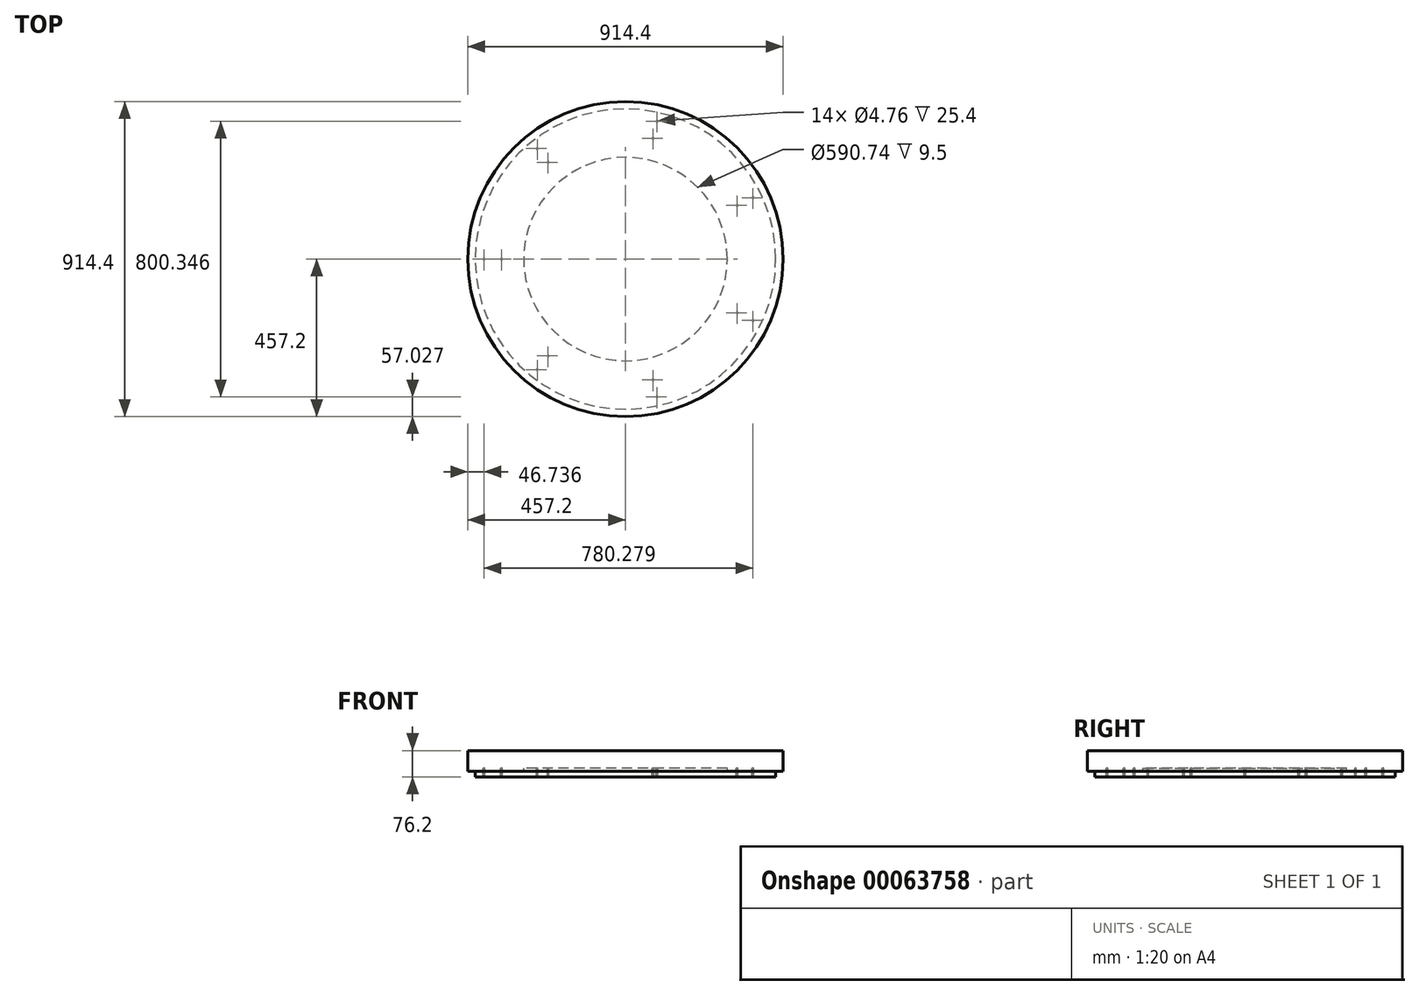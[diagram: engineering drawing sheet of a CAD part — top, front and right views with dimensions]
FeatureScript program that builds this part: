
annotation { "Feature Type Name" : "Feature", "Feature Type Description" : "" }
export const myFeature = defineFeature(function(context is Context, id is Id, definition is map)
    precondition{}
    {
        {
            assignVariable(context, id + "F0", {"name" : "H", "anyValue" : 15});
        }
        {
            assignVariable(context, id + "F1", {"name" : "S", "anyValue" : 7});
        }
        {
            var Q0;
            Q0=qCreatedBy(makeId("Top.planeOp"),FACE);
            var sketch = newSketch(context, id + "F2", { "sketchPlane" : qUnion([Q0])});
            skCircle(sketch, "E0", {"center": v(0, 0) * mm, "radius": 457.2 * mm});
            skCircle(sketch, "E1", {"center": v(0, 0) * mm, "radius": 444.5 * mm});
            skCircle(sketch, "E2.0", {"center": v(0, 0) * mm, "radius": 435.86 * mm});
            skSolve(sketch);
        }
        {
            var Q0;
            Q0=makeQuery(id+"F2.imprint","IMPRINT",FACE,{"disambiguationData":[TD([[makeQuery(id+"F2.imprint","IMPRINT",EDGE,{"derivedFrom":sQuery(id+"F2.wireOp",EDGE,"E1")}),1.0]])]});
            var Q1;
            Q1=sQuery(id+"F2.wireOp",EDGE,"E1");
            var Q2;
            Q2=sQuery(id+"F2.wireOp",EDGE,"E2.0");
            extrude(context, id + "F3", {"entities" : qUnion([Q0]), "surfaceEntities" : qUnion([Q1, Q2]), "depth" : (getVariable(context, 'H') - 5.5) * mm});
        }
        {
            var Q0;
            Q0=makeQuery(id+"F3.opExtrude","CAP_FACE",FACE,{"disambiguationData":[OSD([sQuery(id+"F2.wireOp",EDGE,"E1"),sQuery(id+"F2.wireOp",EDGE,"E2.0")])],"isStart":false});
            var sketch = newSketch(context, id + "F4", { "sketchPlane" : qUnion([Q0])});
            skCircle(sketch, "E3.0", {"center": v(0, 0) * mm, "radius": 435.86 * mm});
            skSolve(sketch);
        }
        {
            var Q0;
            Q0=qSketchRegion(id+"F4",true);
            extrude(context, id + "F5", {"entities" : qUnion([Q0]), "oppositeDirection" : true, "depth" : 25.4 * mm});
        }
        {
            var Q0;
            Q0=makeQuery(id+"F5.opExtrude","CAP_FACE",FACE,{"disambiguationData":[OSD([sQuery(id+"F4.wireOp",EDGE,"E3.0")])],"isStart":true});
            var sketch = newSketch(context, id + "F6", { "sketchPlane" : qUnion([Q0])});
            skLineSegment(sketch, "E4", {"start": v(-435.86, 0) * mm, "end": v(0, 0) * mm, "construction": true});
            skCircle(sketch, "E5.0", {"center": v(0, 0) * mm, "radius": 410.46 * mm, "construction": true});
            skCircle(sketch, "E6.0", {"center": v(0, 0) * mm, "radius": 359.66 * mm, "construction": true});
            skPoint(sketch, "E7", {"position": v(-410.46, 0) * mm});
            skPoint(sketch, "E8", {"position": v(-359.66, 0) * mm});
            skPoint(sketch, "E9.1.0", {"position": v(-224.25, -281.2) * mm});
            skPoint(sketch, "E9.1.1", {"position": v(-255.92, -320.91) * mm});
            skPoint(sketch, "E9.2.0", {"position": v(80.03, -350.65) * mm});
            skPoint(sketch, "E9.2.1", {"position": v(91.34, -400.17) * mm});
            skPoint(sketch, "E9.3.0", {"position": v(324.05, -156.05) * mm});
            skPoint(sketch, "E9.3.1", {"position": v(369.82, -178.1) * mm});
            skPoint(sketch, "E9.4.0", {"position": v(324.05, 156.05) * mm});
            skPoint(sketch, "E9.4.1", {"position": v(369.82, 178.1) * mm});
            skPoint(sketch, "E10.0.5.0", {"position": v(80.03, 350.65) * mm});
            skPoint(sketch, "E10.1.5.0", {"position": v(91.34, 400.17) * mm});
            skPoint(sketch, "E11.0.6.0", {"position": v(-224.25, 281.2) * mm});
            skPoint(sketch, "E11.1.6.0", {"position": v(-255.92, 320.91) * mm});
            skSolve(sketch);
        }
        {
            var Q0;
            Q0=sQuery(id+"F6.wireOp",VERTEX,"E7");
            var Q1;
            Q1=sQuery(id+"F6.wireOp",VERTEX,"E8");
            var Q2;
            Q2=sQuery(id+"F6.wireOp",VERTEX,"E9.4.1");
            var Q3;
            Q3=sQuery(id+"F6.wireOp",VERTEX,"E9.4.0");
            var Q4;
            Q4=sQuery(id+"F6.wireOp",VERTEX,"E9.3.0");
            var Q5;
            Q5=sQuery(id+"F6.wireOp",VERTEX,"E9.3.1");
            var Q6;
            Q6=sQuery(id+"F6.wireOp",VERTEX,"E9.2.0");
            var Q7;
            Q7=sQuery(id+"F6.wireOp",VERTEX,"E9.2.1");
            var Q8;
            Q8=sQuery(id+"F6.wireOp",VERTEX,"E9.1.1");
            var Q9;
            Q9=sQuery(id+"F6.wireOp",VERTEX,"E9.1.0");
            var Q10;
            Q10=sQuery(id+"F6.wireOp",VERTEX,"E10.0.5.0");
            var Q11;
            Q11=sQuery(id+"F6.wireOp",VERTEX,"E10.1.5.0");
            var Q12;
            Q12=sQuery(id+"F6.wireOp",VERTEX,"E11.1.6.0");
            var Q13;
            Q13=sQuery(id+"F6.wireOp",VERTEX,"E11.0.6.0");
            var Q14;
            Q14=makeQuery(id+"F5.opExtrude","SWEPT_BODY",BODY,{"disambiguationData":[OSD([sQuery(id+"F4.wireOp",EDGE,"E3.0")])]});
            hole(context, id + "F7", {"style" : HoleStyle.C_SINK, "holeDiameter" : 4.76 * mm, "cSinkDiameter" : 8.43 * mm, "endStyle" : HoleEndStyle.THROUGH, "locations" : qUnion([Q0, Q1, Q2, Q3, Q4, Q5, Q6, Q7, Q8, Q9, Q10, Q11, Q12, Q13]), "scope" : qUnion([Q14]), "cSinkAngle" : 90 * degree});
        }
        {
            var Q0;
            Q0=makeQuery(id+"F5.opExtrude","SWEPT_BODY",BODY,{"disambiguationData":[OSD([sQuery(id+"F4.wireOp",EDGE,"E3.0")])]});
            var Q1;
            Q1=qCreatedBy(makeId("Top.planeOp"),FACE);
            mirror(context, id + "F8", {"entities" : qUnion([Q0]), "mirrorPlane" : qUnion([Q1])});
        }
        {
            var Q0;
            Q0=makeQuery(id+"F8.opPattern","COPY",BODY,{"derivedFrom":makeQuery(id+"F5.opExtrude","SWEPT_BODY",BODY,{"disambiguationData":[OSD([sQuery(id+"F4.wireOp",EDGE,"E3.0")])]}),"instanceName":"1"});
            var Q1;
            Q1=makeQuery(id+"F5.opExtrude","CAP_FACE",FACE,{"disambiguationData":[OSD([sQuery(id+"F4.wireOp",EDGE,"E3.0")])],"isStart":true});
            transform(context, id + "F9", {"entities" : qUnion([Q0]), "transformType" : TransformType.TRANSLATION_3D, "dx" : 0 * mm, "dy" : 0 * mm, "dz" : (getVariable(context, 'H') - 5.5) * mm, "makeCopy" : false});
        }
        {
            var Q0;
            Q0=makeQuery(id+"F8.opPattern","COPY",FACE,{"derivedFrom":makeQuery(id+"F5.opExtrude","CAP_FACE",FACE,{"disambiguationData":[OSD([sQuery(id+"F4.wireOp",EDGE,"E3.0")])],"isStart":true}),"instanceName":"1"});
            var sketch = newSketch(context, id + "F10", { "sketchPlane" : qUnion([Q0])});
            skCircle(sketch, "E12.0", {"center": v(0, 0) * mm, "radius": 417.6 * mm, "construction": true});
            skCircle(sketch, "E13.0", {"center": v(0, 0) * mm, "radius": 381.1 * mm, "construction": true});
            skCircle(sketch, "E14.0", {"center": v(0, 0) * mm, "radius": 344.58 * mm, "construction": true});
            skLineSegment(sketch, "E15", {"start": v(0, 0) * mm, "end": v(0, 417.6) * mm, "construction": true});
            skLineSegment(sketch, "E16.0", {"start": v(22.23, 0) * mm, "end": v(22.23, 265.2) * mm, "construction": true});
            skLineSegment(sketch, "E17.0", {"start": v(-22.23, 0) * mm, "end": v(-22.23, 265.2) * mm, "construction": true});
            skPoint(sketch, "E18", {"position": v(-22.23, 380.45) * mm});
            skPoint(sketch, "E19", {"position": v(-22.23, 343.87) * mm});
            skPoint(sketch, "E20", {"position": v(22.23, 343.87) * mm});
            skPoint(sketch, "E21", {"position": v(22.23, 380.45) * mm});
            skPoint(sketch, "E22", {"position": v(22.23, 417.02) * mm});
            skPoint(sketch, "E23", {"position": v(-22.23, 417.02) * mm});
            skPoint(sketch, "E24.1.0", {"position": v(-333.9, 85.12) * mm});
            skPoint(sketch, "E24.1.1", {"position": v(-368.7, 96.43) * mm});
            skPoint(sketch, "E24.1.2", {"position": v(-403.47, 107.73) * mm});
            skPoint(sketch, "E24.1.3", {"position": v(-389.74, 150) * mm});
            skPoint(sketch, "E24.1.4", {"position": v(-354.96, 138.7) * mm});
            skPoint(sketch, "E24.1.5", {"position": v(-320.17, 127.4) * mm});
            skPoint(sketch, "E24.2.0", {"position": v(-184.14, -291.26) * mm});
            skPoint(sketch, "E24.2.1", {"position": v(-205.64, -320.85) * mm});
            skPoint(sketch, "E24.2.2", {"position": v(-227.14, -350.44) * mm});
            skPoint(sketch, "E24.2.3", {"position": v(-263.1, -324.3) * mm});
            skPoint(sketch, "E24.2.4", {"position": v(-241.6, -294.72) * mm});
            skPoint(sketch, "E24.2.5", {"position": v(-220.1, -265.13) * mm});
            skPoint(sketch, "E24.3.0", {"position": v(220.1, -265.13) * mm});
            skPoint(sketch, "E24.3.1", {"position": v(241.6, -294.72) * mm});
            skPoint(sketch, "E24.3.2", {"position": v(263.1, -324.3) * mm});
            skPoint(sketch, "E24.3.3", {"position": v(227.14, -350.44) * mm});
            skPoint(sketch, "E24.3.4", {"position": v(205.64, -320.85) * mm});
            skPoint(sketch, "E24.3.5", {"position": v(184.14, -291.26) * mm});
            skPoint(sketch, "E24.4.0", {"position": v(320.17, 127.4) * mm});
            skPoint(sketch, "E24.4.1", {"position": v(354.96, 138.7) * mm});
            skPoint(sketch, "E24.4.2", {"position": v(389.74, 150) * mm});
            skPoint(sketch, "E24.4.3", {"position": v(403.47, 107.73) * mm});
            skPoint(sketch, "E24.4.4", {"position": v(368.7, 96.43) * mm});
            skPoint(sketch, "E24.4.5", {"position": v(333.9, 85.12) * mm});
            skSolve(sketch);
        }
        {
            var Q0;
            Q0=sQuery(id+"F10.wireOp",VERTEX,"E23");
            var Q1;
            Q1=sQuery(id+"F10.wireOp",VERTEX,"E18");
            var Q2;
            Q2=sQuery(id+"F10.wireOp",VERTEX,"E19");
            var Q3;
            Q3=sQuery(id+"F10.wireOp",VERTEX,"E20");
            var Q4;
            Q4=sQuery(id+"F10.wireOp",VERTEX,"E21");
            var Q5;
            Q5=sQuery(id+"F10.wireOp",VERTEX,"E22");
            var Q6;
            Q6=sQuery(id+"F10.wireOp",VERTEX,"E24.4.0");
            var Q7;
            Q7=sQuery(id+"F10.wireOp",VERTEX,"E24.4.1");
            var Q8;
            Q8=sQuery(id+"F10.wireOp",VERTEX,"E24.4.2");
            var Q9;
            Q9=sQuery(id+"F10.wireOp",VERTEX,"E24.4.3");
            var Q10;
            Q10=sQuery(id+"F10.wireOp",VERTEX,"E24.4.4");
            var Q11;
            Q11=sQuery(id+"F10.wireOp",VERTEX,"E24.4.5");
            var Q12;
            Q12=sQuery(id+"F10.wireOp",VERTEX,"E24.3.0");
            var Q13;
            Q13=sQuery(id+"F10.wireOp",VERTEX,"E24.3.1");
            var Q14;
            Q14=sQuery(id+"F10.wireOp",VERTEX,"E24.3.2");
            var Q15;
            Q15=sQuery(id+"F10.wireOp",VERTEX,"E24.3.3");
            var Q16;
            Q16=sQuery(id+"F10.wireOp",VERTEX,"E24.3.4");
            var Q17;
            Q17=sQuery(id+"F10.wireOp",VERTEX,"E24.3.5");
            var Q18;
            Q18=sQuery(id+"F10.wireOp",VERTEX,"E24.2.2");
            var Q19;
            Q19=sQuery(id+"F10.wireOp",VERTEX,"E24.2.1");
            var Q20;
            Q20=sQuery(id+"F10.wireOp",VERTEX,"E24.2.0");
            var Q21;
            Q21=sQuery(id+"F10.wireOp",VERTEX,"E24.2.5");
            var Q22;
            Q22=sQuery(id+"F10.wireOp",VERTEX,"E24.2.4");
            var Q23;
            Q23=sQuery(id+"F10.wireOp",VERTEX,"E24.2.3");
            var Q24;
            Q24=sQuery(id+"F10.wireOp",VERTEX,"E24.1.0");
            var Q25;
            Q25=sQuery(id+"F10.wireOp",VERTEX,"E24.1.5");
            var Q26;
            Q26=sQuery(id+"F10.wireOp",VERTEX,"E24.1.1");
            var Q27;
            Q27=sQuery(id+"F10.wireOp",VERTEX,"E24.1.2");
            var Q28;
            Q28=sQuery(id+"F10.wireOp",VERTEX,"E24.1.3");
            var Q29;
            Q29=sQuery(id+"F10.wireOp",VERTEX,"E24.1.4");
            var Q30;
            Q30=makeQuery(id+"F8.opPattern","COPY",BODY,{"derivedFrom":makeQuery(id+"F5.opExtrude","SWEPT_BODY",BODY,{"disambiguationData":[OSD([sQuery(id+"F4.wireOp",EDGE,"E3.0")])]}),"instanceName":"1"});
            hole(context, id + "F11", {"style" : HoleStyle.SIMPLE, "holeDiameter" : 3.17 * mm, "endStyle" : HoleEndStyle.BLIND, "holeDepth" : 3.17 * mm, "locations" : qUnion([Q0, Q1, Q2, Q3, Q4, Q5, Q6, Q7, Q8, Q9, Q10, Q11, Q12, Q13, Q14, Q15, Q16, Q17, Q18, Q19, Q20, Q21, Q22, Q23, Q24, Q25, Q26, Q27, Q28, Q29]), "scope" : qUnion([Q30])});
        }
        {
            var Q0;
            Q0=makeQuery(id+"F8.opPattern","COPY",FACE,{"derivedFrom":makeQuery(id+"F5.opExtrude","CAP_FACE",FACE,{"disambiguationData":[OSD([sQuery(id+"F4.wireOp",EDGE,"E3.0")])],"isStart":false}),"instanceName":"1"});
            var sketch = newSketch(context, id + "F12", { "sketchPlane" : qUnion([Q0])});
            skCircle(sketch, "E25", {"center": v(0, 0) * mm, "radius": 295.37 * mm});
            skSolve(sketch);
        }
        {
            var Q0;
            Q0=qSketchRegion(id+"F12",true);
            extrude(context, id + "F13", {"entities" : qUnion([Q0]), "operationType" : NewBodyOperationType.REMOVE, "oppositeDirection" : true, "depth" : 25.4 * mm});
        }
        {
            var Q0;
            Q0=makeQuery(id+"F8.opPattern","COPY",FACE,{"derivedFrom":makeQuery(id+"F5.opExtrude","CAP_FACE",FACE,{"disambiguationData":[OSD([sQuery(id+"F4.wireOp",EDGE,"E3.0")])],"isStart":false}),"instanceName":"1"});
            var sketch = newSketch(context, id + "F14", { "sketchPlane" : qUnion([Q0])});
            skLineSegment(sketch, "E26", {"start": v(-410.46, 0) * mm, "end": v(-359.66, 0) * mm, "construction": true});
            skLineSegment(sketch, "E27.0", {"start": v(-435.86, 12.7) * mm, "end": v(-334.26, 12.7) * mm});
            skLineSegment(sketch, "E28.0", {"start": v(-435.86, -12.7) * mm, "end": v(-334.26, -12.7) * mm});
            skLineSegment(sketch, "E29", {"start": v(-435.86, -12.7) * mm, "end": v(-435.86, 12.7) * mm});
            skLineSegment(sketch, "E30", {"start": v(-334.26, -12.7) * mm, "end": v(-334.26, 12.7) * mm});
            skSolve(sketch);
        }
        {
            var Q0;
            Q0=qSketchRegion(id+"F14",true);
            extrude(context, id + "F15", {"entities" : qUnion([Q0]), "depth" : (getVariable(context, 'H') - 7.5) * mm});
        }
        {
            var Q0;
            Q0=makeQuery(id+"F15.opExtrude","SWEPT_BODY",BODY,{"disambiguationData":[OSD([sQuery(id+"F14.wireOp",EDGE,"E27.0"),sQuery(id+"F14.wireOp",EDGE,"E28.0"),sQuery(id+"F14.wireOp",EDGE,"E29"),sQuery(id+"F14.wireOp",EDGE,"E30")])]});
            var Q1;
            Q1=makeQuery(id+"F8.opPattern","COPY",EDGE,{"derivedFrom":makeQuery(id+"F5.opExtrude","CAP_EDGE",EDGE,{"disambiguationData":[OSD([sQuery(id+"F4.wireOp",EDGE,"E3.0")])],"isStart":false}),"instanceName":"1"});
            circularPattern(context, id + "F16", {"entities" : qUnion([Q0]), "axis" : qUnion([Q1]), "angle" : 360 * degree, "instanceCount" : getVariable(context, 'S'), "equalSpace" : true});
        }
        {
            var Q0;
            Q0=makeQuery(id+"F2.imprint","IMPRINT",FACE,{"disambiguationData":[TD([[makeQuery(id+"F2.imprint","IMPRINT",EDGE,{"derivedFrom":sQuery(id+"F2.wireOp",EDGE,"E0")}),1.0]])]});
            extrude(context, id + "F17", {"entities" : qUnion([Q0]), "depth" : (getVariable(context, 'H') - 5.5) * mm});
        }
        {
            var Q0;
            Q0=makeQuery(id+"F17.opExtrude","CAP_FACE",FACE,{"disambiguationData":[OSD([sQuery(id+"F2.wireOp",EDGE,"E0"),sQuery(id+"F2.wireOp",EDGE,"E1")])],"isStart":false});
            var sketch = newSketch(context, id + "F18", { "sketchPlane" : qUnion([Q0])});
            skCircle(sketch, "E31.0", {"center": v(0, 0) * mm, "radius": 457.2 * mm});
            skSolve(sketch);
        }
        {
            var Q0;
            Q0=qSketchRegion(id+"F18",true);
            extrude(context, id + "F19", {"entities" : qUnion([Q0]), "operationType" : NewBodyOperationType.ADD, "depth" : 50.8 * mm});
        }
    });
